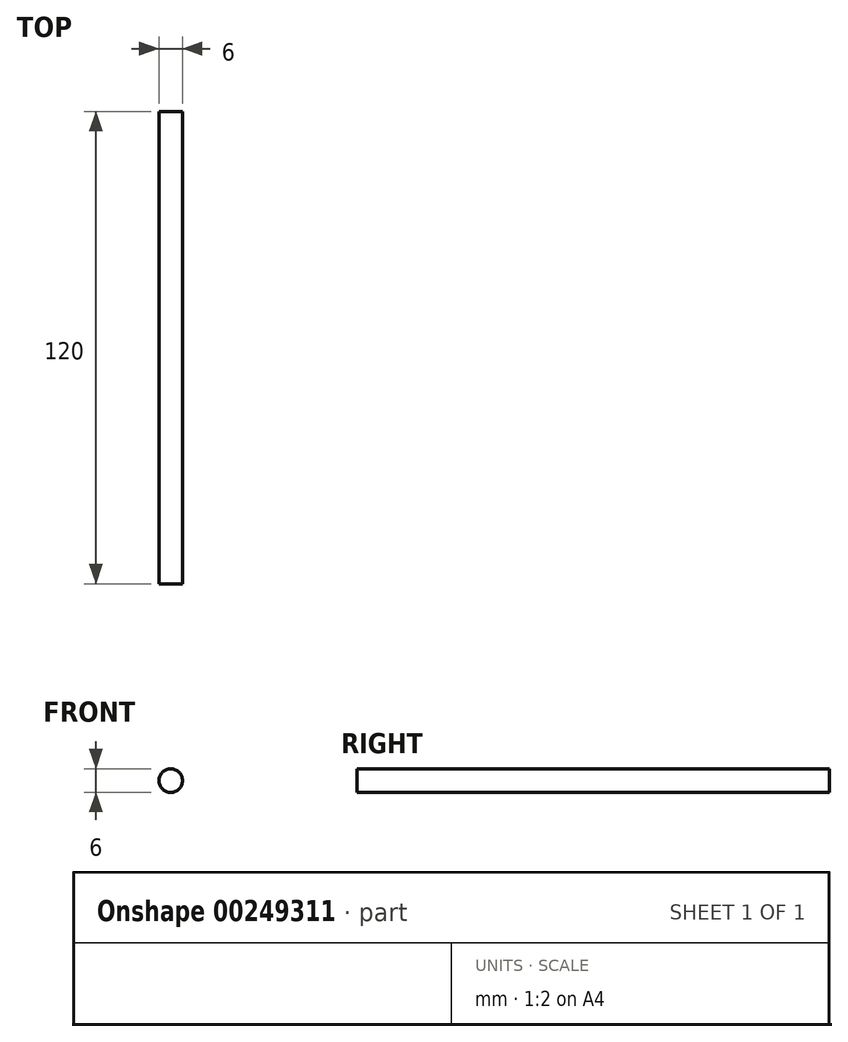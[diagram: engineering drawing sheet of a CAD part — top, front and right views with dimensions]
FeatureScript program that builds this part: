
annotation { "Feature Type Name" : "Feature", "Feature Type Description" : "" }
export const myFeature = defineFeature(function(context is Context, id is Id, definition is map)
    precondition{}
    {
        {
            var Q0;
            Q0=qCreatedBy(makeId("Front.planeOp"),FACE);
            var sketch = newSketch(context, id + "F0", { "sketchPlane" : qUnion([Q0])});
            skCircle(sketch, "E0", {"center": v(0, 0) * mm, "radius": 3 * mm});
            skSolve(sketch);
        }
        {
            var Q0;
            Q0=makeQuery(id+"F0.imprint","IMPRINT",FACE,{"disambiguationData":[TD([[makeQuery(id+"F0.imprint","IMPRINT",EDGE,{"derivedFrom":sQuery(id+"F0.wireOp",EDGE,"E0")}),1.0]])]});
            extrude(context, id + "F1", {"entities" : qUnion([Q0]), "depth" : 120 * mm, "offsetDistance" : 25 * mm});
        }
    });
